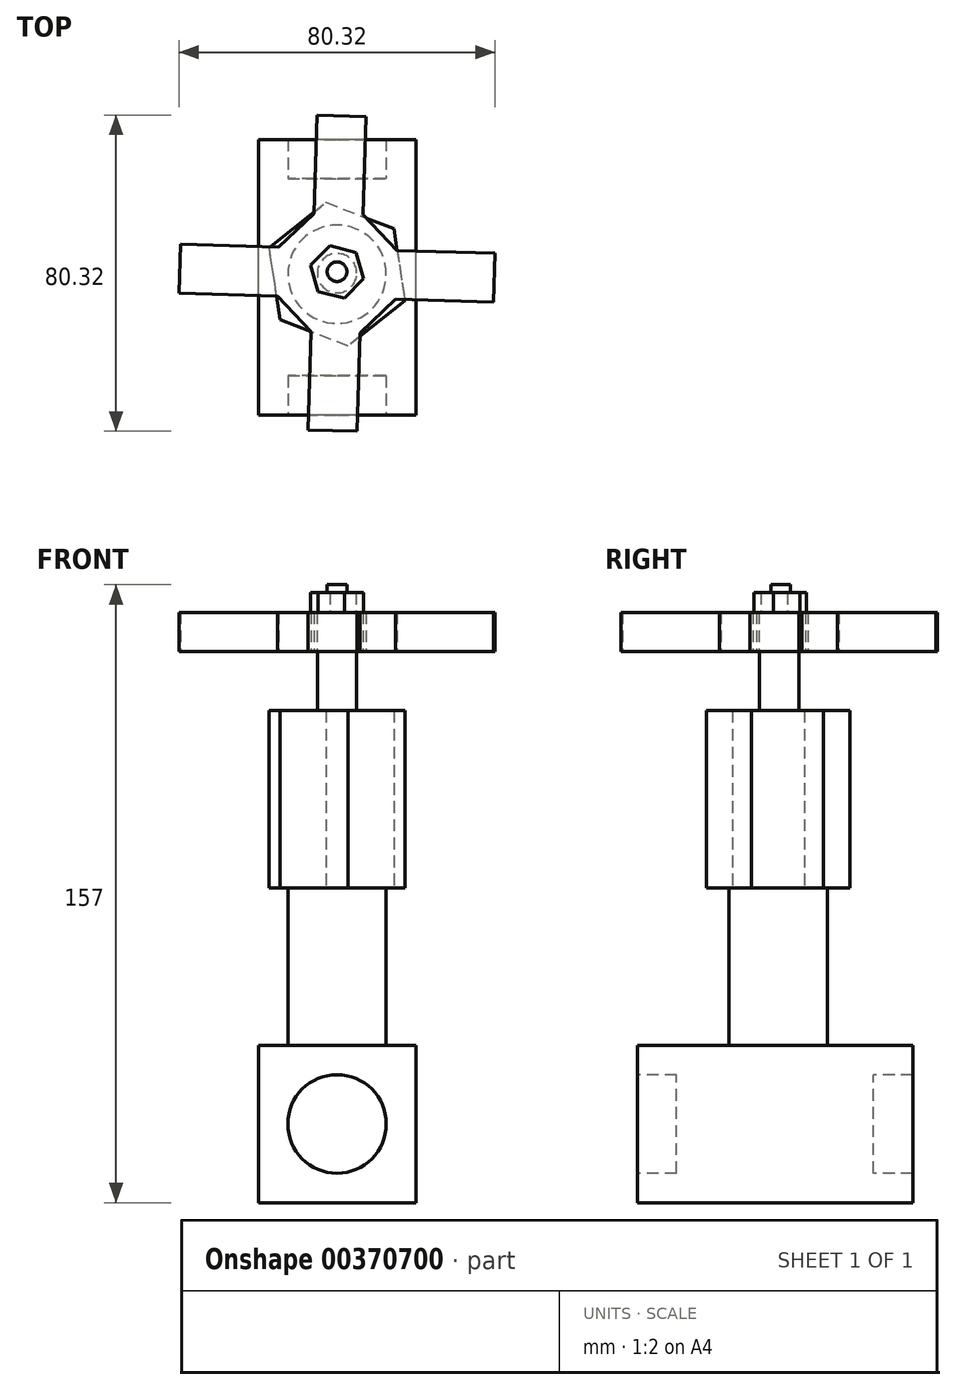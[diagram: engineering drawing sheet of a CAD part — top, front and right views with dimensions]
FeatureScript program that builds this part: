
annotation { "Feature Type Name" : "Feature", "Feature Type Description" : "" }
export const myFeature = defineFeature(function(context is Context, id is Id, definition is map)
    precondition{}
    {
        {
            var Q0;
            Q0=qCreatedBy(makeId("Front.planeOp"),FACE);
            var sketch = newSketch(context, id + "F0", { "sketchPlane" : qUnion([Q0])});
            skLineSegment(sketch, "E0.bottom", {"start": v(20, 20) * mm, "end": v(-20, 20) * mm});
            skLineSegment(sketch, "E0.top", {"start": v(20, -20) * mm, "end": v(-20, -20) * mm});
            skLineSegment(sketch, "E0.left", {"start": v(20, 20) * mm, "end": v(20, -20) * mm});
            skLineSegment(sketch, "E0.right", {"start": v(-20, 20) * mm, "end": v(-20, -20) * mm});
            skPoint(sketch, "E0.middle", {"position": v(0, 0) * mm});
            skSolve(sketch);
        }
        {
            var Q0;
            Q0=makeQuery(id+"F0.imprint","IMPRINT",FACE,{"disambiguationData":[TD([[makeQuery(id+"F0.imprint","IMPRINT",EDGE,{"derivedFrom":sQuery(id+"F0.wireOp",EDGE,"E0.bottom")}),1.0]])]});
            extrude(context, id + "F1", {"entities" : qUnion([Q0]), "depth" : 70 * mm});
        }
        {
            var Q0;
            Q0=qCreatedBy(makeId("Front.planeOp"),FACE);
            var sketch = newSketch(context, id + "F2", { "sketchPlane" : qUnion([Q0])});
            skCircle(sketch, "E1", {"center": v(0, 0) * mm, "radius": 12.5 * mm});
            skSolve(sketch);
        }
        {
            var Q0;
            Q0 = qSketchRegion(id + "F2", true);
            extrude(context, id + "F3", {"entities" : qUnion([Q0]), "operationType" : NewBodyOperationType.REMOVE, "endBound" : BoundingType.SYMMETRIC, "oppositeDirection" : true, "depth" : 20 * mm});
        }
        {
            var Q0;
            Q0=makeQuery(id+"F1.opExtrude","CAP_FACE",FACE,{"disambiguationData":[OSD([sQuery(id+"F0.wireOp",EDGE,"E0.bottom"),sQuery(id+"F0.wireOp",EDGE,"E0.top"),sQuery(id+"F0.wireOp",EDGE,"E0.left"),sQuery(id+"F0.wireOp",EDGE,"E0.right")])],"isStart":false});
            var sketch = newSketch(context, id + "F4", { "sketchPlane" : qUnion([Q0])});
            skCircle(sketch, "E2", {"center": v(0, 0) * mm, "radius": 12.5 * mm});
            skSolve(sketch);
        }
        {
            var Q0;
            Q0 = qSketchRegion(id + "F4", true);
            extrude(context, id + "F5", {"entities" : qUnion([Q0]), "operationType" : NewBodyOperationType.REMOVE, "endBound" : BoundingType.SYMMETRIC, "oppositeDirection" : true, "depth" : 20 * mm});
        }
        {
            var Q0;
            Q0=makeQuery(id+"F1.opExtrude","SWEPT_FACE",FACE,{"disambiguationData":[OSD([sQuery(id+"F0.wireOp",EDGE,"E0.bottom")])]});
            var sketch = newSketch(context, id + "F6", { "sketchPlane" : qUnion([Q0])});
            skCircle(sketch, "E3", {"center": v(0, -34.23) * mm, "radius": 12.5 * mm});
            skSolve(sketch);
        }
        {
            var Q0;
            Q0 = qSketchRegion(id + "F6", true);
            extrude(context, id + "F7", {"entities" : qUnion([Q0]), "operationType" : NewBodyOperationType.ADD, "depth" : 40 * mm});
        }
        {
            var Q0;
            Q0=makeQuery(id+"F7.opExtrude","CAP_FACE",FACE,{"disambiguationData":[OSD([sQuery(id+"F6.wireOp",EDGE,"E3")])],"isStart":false});
            var sketch = newSketch(context, id + "F8", { "sketchPlane" : qUnion([Q0])});
            skCircle(sketch, "E4.cCircle", {"center": v(0, -34.23) * mm, "radius": 16 * mm, "construction": true});
            skLineSegment(sketch, "E4.0", {"start": v(-17.2, -27.5) * mm, "end": v(-2.78, -15.96) * mm});
            skLineSegment(sketch, "E4.1", {"start": v(-2.78, -15.96) * mm, "end": v(14.43, -22.69) * mm});
            skLineSegment(sketch, "E4.2", {"start": v(14.43, -22.69) * mm, "end": v(17.2, -40.95) * mm});
            skLineSegment(sketch, "E4.3", {"start": v(17.2, -40.95) * mm, "end": v(2.78, -52.5) * mm});
            skLineSegment(sketch, "E4.4", {"start": v(2.78, -52.5) * mm, "end": v(-14.43, -45.77) * mm});
            skLineSegment(sketch, "E4.5", {"start": v(-14.43, -45.77) * mm, "end": v(-17.2, -27.5) * mm});
            skPoint(sketch, "E4.0.midPoint", {"position": v(-10, -21.74) * mm});
            skSolve(sketch);
        }
        {
            var Q0;
            Q0 = qSketchRegion(id + "F8", true);
            extrude(context, id + "F9", {"entities" : qUnion([Q0]), "operationType" : NewBodyOperationType.ADD, "depth" : 45 * mm});
        }
        {
            var Q0;
            Q0=makeQuery(id+"F9.opExtrude","CAP_FACE",FACE,{"disambiguationData":[OSD([sQuery(id+"F8.wireOp",EDGE,"E4.0"),sQuery(id+"F8.wireOp",EDGE,"E4.1"),sQuery(id+"F8.wireOp",EDGE,"E4.2"),sQuery(id+"F8.wireOp",EDGE,"E4.3"),sQuery(id+"F8.wireOp",EDGE,"E4.4"),sQuery(id+"F8.wireOp",EDGE,"E4.5")])],"isStart":false});
            var sketch = newSketch(context, id + "F10", { "sketchPlane" : qUnion([Q0])});
            skCircle(sketch, "E5", {"center": v(0, -33.96) * mm, "radius": 5 * mm});
            skSolve(sketch);
        }
        {
            var Q0;
            Q0 = qSketchRegion(id + "F10", true);
            extrude(context, id + "F11", {"entities" : qUnion([Q0]), "operationType" : NewBodyOperationType.ADD, "depth" : 15 * mm});
        }
        {
            var Q0;
            Q0=makeQuery(id+"F11.opExtrude","CAP_FACE",FACE,{"disambiguationData":[OSD([sQuery(id+"F10.wireOp",EDGE,"E5")])],"isStart":false});
            var sketch = newSketch(context, id + "F12", { "sketchPlane" : qUnion([Q0])});
            skCircle(sketch, "E6.cCircle", {"center": v(0, -33.96) * mm, "radius": 15 * mm, "construction": true});
            skLineSegment(sketch, "E6.0", {"start": v(6.64, -19.15) * mm, "end": v(15.17, -28.18) * mm});
            skLineSegment(sketch, "E6.1", {"start": v(15.17, -28.18) * mm, "end": v(14.82, -40.6) * mm});
            skLineSegment(sketch, "E6.2", {"start": v(14.82, -40.6) * mm, "end": v(5.78, -49.13) * mm});
            skLineSegment(sketch, "E6.3", {"start": v(5.78, -49.13) * mm, "end": v(-6.64, -48.78) * mm});
            skLineSegment(sketch, "E6.4", {"start": v(-6.64, -48.78) * mm, "end": v(-15.17, -39.75) * mm});
            skLineSegment(sketch, "E6.5", {"start": v(-15.17, -39.75) * mm, "end": v(-14.82, -27.32) * mm});
            skLineSegment(sketch, "E6.6", {"start": v(-14.82, -27.32) * mm, "end": v(-5.78, -18.8) * mm});
            skLineSegment(sketch, "E6.7", {"start": v(-5.78, -18.8) * mm, "end": v(6.64, -19.15) * mm});
            skPoint(sketch, "E6.0.midPoint", {"position": v(10.9, -23.66) * mm});
            skSolve(sketch);
        }
        {
            var Q0;
            Q0 = qSketchRegion(id + "F12", true);
            extrude(context, id + "F13", {"entities" : qUnion([Q0]), "operationType" : NewBodyOperationType.ADD, "depth" : 10 * mm});
        }
        {
            var Q0;
            Q0=makeQuery(id+"F13.opExtrude","SWEPT_FACE",FACE,{"disambiguationData":[OSD([sQuery(id+"F12.wireOp",EDGE,"E6.3")])]});
            var sketch = newSketch(context, id + "F14", { "sketchPlane" : qUnion([Q0])});
            skLineSegment(sketch, "E7.bottom", {"start": v(-5.24, 130) * mm, "end": v(7.18, 130) * mm});
            skLineSegment(sketch, "E7.top", {"start": v(-5.24, 120) * mm, "end": v(7.18, 120) * mm});
            skLineSegment(sketch, "E7.left", {"start": v(-5.24, 130) * mm, "end": v(-5.24, 120) * mm});
            skLineSegment(sketch, "E7.right", {"start": v(7.18, 130) * mm, "end": v(7.18, 120) * mm});
            skSolve(sketch);
        }
        {
            var Q0;
            Q0 = qSketchRegion(id + "F14", true);
            extrude(context, id + "F15", {"entities" : qUnion([Q0]), "operationType" : NewBodyOperationType.ADD, "depth" : 25 * mm});
        }
        {
            var Q0;
            Q0=makeQuery(id+"F13.opExtrude","SWEPT_FACE",FACE,{"disambiguationData":[OSD([sQuery(id+"F12.wireOp",EDGE,"E6.1")])]});
            var sketch = newSketch(context, id + "F16", { "sketchPlane" : qUnion([Q0])});
            skLineSegment(sketch, "E8.bottom", {"start": v(-40.16, 130) * mm, "end": v(-27.74, 130) * mm});
            skLineSegment(sketch, "E8.top", {"start": v(-40.16, 120) * mm, "end": v(-27.74, 120) * mm});
            skLineSegment(sketch, "E8.left", {"start": v(-40.16, 130) * mm, "end": v(-40.16, 120) * mm});
            skLineSegment(sketch, "E8.right", {"start": v(-27.74, 130) * mm, "end": v(-27.74, 120) * mm});
            skSolve(sketch);
        }
        {
            var Q0;
            Q0 = qSketchRegion(id + "F16", true);
            extrude(context, id + "F17", {"entities" : qUnion([Q0]), "operationType" : NewBodyOperationType.ADD, "depth" : 25 * mm});
        }
        {
            var Q0;
            Q0=makeQuery(id+"F13.opExtrude","SWEPT_FACE",FACE,{"disambiguationData":[OSD([sQuery(id+"F12.wireOp",EDGE,"E6.5")])]});
            var sketch = newSketch(context, id + "F18", { "sketchPlane" : qUnion([Q0])});
            skLineSegment(sketch, "E9.bottom", {"start": v(27.74, 120) * mm, "end": v(40.16, 120) * mm});
            skLineSegment(sketch, "E9.top", {"start": v(27.74, 130) * mm, "end": v(40.16, 130) * mm});
            skLineSegment(sketch, "E9.left", {"start": v(27.74, 120) * mm, "end": v(27.74, 130) * mm});
            skLineSegment(sketch, "E9.right", {"start": v(40.16, 120) * mm, "end": v(40.16, 130) * mm});
            skSolve(sketch);
        }
        {
            var Q0;
            Q0 = qSketchRegion(id + "F18", true);
            extrude(context, id + "F19", {"entities" : qUnion([Q0]), "operationType" : NewBodyOperationType.ADD, "depth" : 25 * mm});
        }
        {
            var Q0;
            Q0=makeQuery(id+"F13.opExtrude","SWEPT_FACE",FACE,{"disambiguationData":[OSD([sQuery(id+"F12.wireOp",EDGE,"E6.7")])]});
            var sketch = newSketch(context, id + "F20", { "sketchPlane" : qUnion([Q0])});
            skLineSegment(sketch, "E10.bottom", {"start": v(5.24, 130) * mm, "end": v(-7.18, 130) * mm});
            skLineSegment(sketch, "E10.top", {"start": v(5.24, 120) * mm, "end": v(-7.18, 120) * mm});
            skLineSegment(sketch, "E10.left", {"start": v(5.24, 130) * mm, "end": v(5.24, 120) * mm});
            skLineSegment(sketch, "E10.right", {"start": v(-7.18, 130) * mm, "end": v(-7.18, 120) * mm});
            skSolve(sketch);
        }
        {
            var Q0;
            Q0 = qSketchRegion(id + "F20", true);
            extrude(context, id + "F21", {"entities" : qUnion([Q0]), "operationType" : NewBodyOperationType.ADD, "depth" : 25 * mm});
        }
        {
            var Q0;
            Q0=makeQuery(id+"F21.boolean.opBoolean","MERGE",FACE,{"derivedFrom":[makeQuery(id+"F19.boolean.opBoolean","MERGE",FACE,{"derivedFrom":[makeQuery(id+"F17.boolean.opBoolean","MERGE",FACE,{"derivedFrom":[makeQuery(id+"F15.boolean.opBoolean","MERGE",FACE,{"derivedFrom":[makeQuery(id+"F13.opExtrude","CAP_FACE",FACE,{"disambiguationData":[OSD([sQuery(id+"F12.wireOp",EDGE,"E6.0"),sQuery(id+"F12.wireOp",EDGE,"E6.1"),sQuery(id+"F12.wireOp",EDGE,"E6.2"),sQuery(id+"F12.wireOp",EDGE,"E6.3"),sQuery(id+"F12.wireOp",EDGE,"E6.4"),sQuery(id+"F12.wireOp",EDGE,"E6.5"),sQuery(id+"F12.wireOp",EDGE,"E6.6"),sQuery(id+"F12.wireOp",EDGE,"E6.7")])],"isStart":false}),makeQuery(id+"F15.opExtrude","SWEPT_FACE",FACE,{"disambiguationData":[OSD([sQuery(id+"F14.wireOp",EDGE,"E7.bottom")])]})]}),makeQuery(id+"F17.opExtrude","SWEPT_FACE",FACE,{"disambiguationData":[OSD([sQuery(id+"F16.wireOp",EDGE,"E8.bottom")])]})]}),makeQuery(id+"F19.opExtrude","SWEPT_FACE",FACE,{"disambiguationData":[OSD([sQuery(id+"F18.wireOp",EDGE,"E9.top")])]})]}),makeQuery(id+"F21.opExtrude","SWEPT_FACE",FACE,{"disambiguationData":[OSD([sQuery(id+"F20.wireOp",EDGE,"E10.bottom")])]})]});
            var sketch = newSketch(context, id + "F22", { "sketchPlane" : qUnion([Q0])});
            skCircle(sketch, "E11.cCircle", {"center": v(0, -33.66) * mm, "radius": 6 * mm, "construction": true});
            skLineSegment(sketch, "E11.0", {"start": v(-6.7, -31.92) * mm, "end": v(-1.84, -26.98) * mm});
            skLineSegment(sketch, "E11.1", {"start": v(-1.84, -26.98) * mm, "end": v(4.86, -28.72) * mm});
            skLineSegment(sketch, "E11.2", {"start": v(4.86, -28.72) * mm, "end": v(6.7, -35.4) * mm});
            skLineSegment(sketch, "E11.3", {"start": v(6.7, -35.4) * mm, "end": v(1.84, -40.34) * mm});
            skLineSegment(sketch, "E11.4", {"start": v(1.84, -40.34) * mm, "end": v(-4.86, -38.6) * mm});
            skLineSegment(sketch, "E11.5", {"start": v(-4.86, -38.6) * mm, "end": v(-6.7, -31.92) * mm});
            skPoint(sketch, "E11.0.midPoint", {"position": v(-4.28, -29.45) * mm});
            skSolve(sketch);
        }
        {
            var Q0;
            Q0 = qSketchRegion(id + "F22", true);
            extrude(context, id + "F23", {"entities" : qUnion([Q0]), "operationType" : NewBodyOperationType.ADD, "depth" : 5 * mm});
        }
        {
            var Q0;
            Q0=makeQuery(id+"F23.opExtrude","CAP_FACE",FACE,{"disambiguationData":[OSD([sQuery(id+"F22.wireOp",EDGE,"E11.0"),sQuery(id+"F22.wireOp",EDGE,"E11.1"),sQuery(id+"F22.wireOp",EDGE,"E11.2"),sQuery(id+"F22.wireOp",EDGE,"E11.3"),sQuery(id+"F22.wireOp",EDGE,"E11.4"),sQuery(id+"F22.wireOp",EDGE,"E11.5")])],"isStart":false});
            var sketch = newSketch(context, id + "F24", { "sketchPlane" : qUnion([Q0])});
            skCircle(sketch, "E12", {"center": v(0, -33.59) * mm, "radius": 2.5 * mm});
            skSolve(sketch);
        }
        {
            var Q0;
            Q0 = qSketchRegion(id + "F24", true);
            extrude(context, id + "F25", {"entities" : qUnion([Q0]), "operationType" : NewBodyOperationType.ADD, "depth" : 2 * mm});
        }
    });
